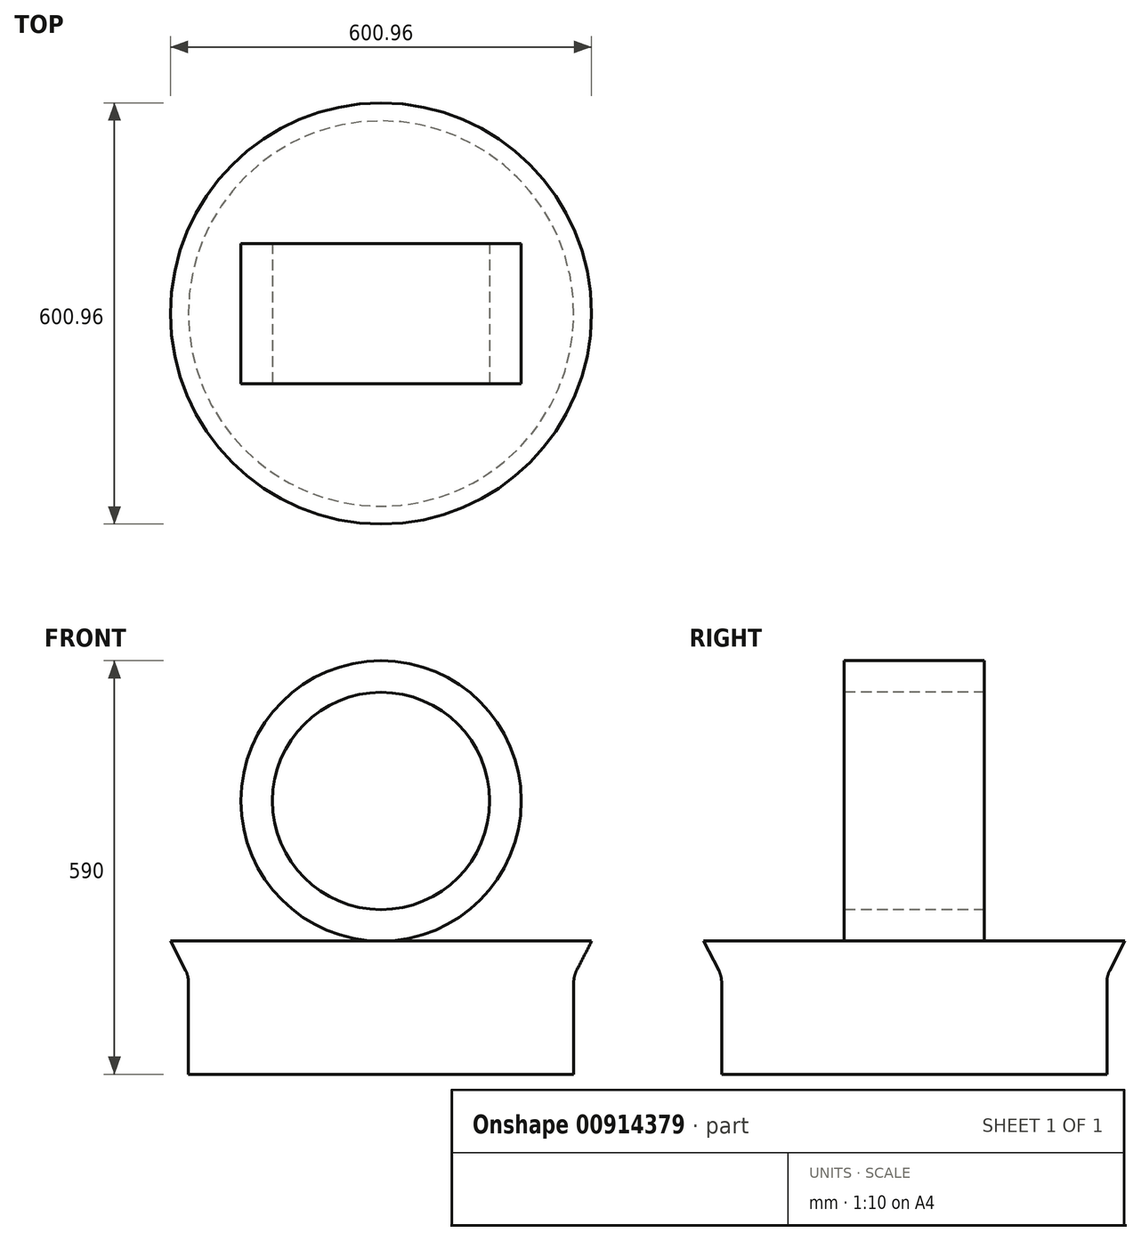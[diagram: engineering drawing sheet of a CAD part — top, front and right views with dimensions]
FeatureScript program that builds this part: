
annotation { "Feature Type Name" : "Feature", "Feature Type Description" : "" }
export const myFeature = defineFeature(function(context is Context, id is Id, definition is map)
    precondition{}
    {
        {
            var Q0;
            Q0=qCreatedBy(makeId("Top.planeOp"),FACE);
            var sketch = newSketch(context, id + "F0", { "sketchPlane" : qUnion([Q0])});
            skCircle(sketch, "E0", {"center": v(0, 0) * mm, "radius": 275 * mm});
            skSolve(sketch);
        }
        {
            var Q0;
            Q0 = qSketchRegion(id + "F0", true);
            extrude(context, id + "F1", {"entities" : qUnion([Q0]), "depth" : 140 * mm, "offsetDistance" : 25 * mm});
        }
        {
            var Q0;
            Q0=makeQuery(id+"F1.opExtrude","CAP_FACE",FACE,{"disambiguationData":[OSD([sQuery(id+"F0.wireOp",EDGE,"E0")])],"isStart":false});
            var sketch = newSketch(context, id + "F2", { "sketchPlane" : qUnion([Q0])});
            skCircle(sketch, "E1", {"center": v(0, 0) * mm, "radius": 275 * mm});
            skSolve(sketch);
        }
        {
            var Q0;
            Q0 = qSketchRegion(id + "F2", true);
            extrude(context, id + "F3", {"entities" : qUnion([Q0]), "operationType" : NewBodyOperationType.ADD, "depth" : 50 * mm, "offsetDistance" : 25 * mm, "hasDraft" : true, "draftAngle" : 27 * degree});
        }
        {
            var Q0;
            Q0=makeQuery(id+"F3.boolean.opBoolean","MERGE",EDGE,{"derivedFrom":[makeQuery(id+"F1.opExtrude","CAP_EDGE",EDGE,{"disambiguationData":[OSD([sQuery(id+"F0.wireOp",EDGE,"E0")])],"isStart":false}),makeQuery(id+"F3.opExtrude","CAP_EDGE",EDGE,{"disambiguationData":[OSD([sQuery(id+"F2.wireOp",EDGE,"E1")])],"isStart":true})]});
            fillet(context, id + "F4", {"entities" : qUnion([Q0]), "radius" : 35.2 * mm, "tangentPropagation" : true, "allowEdgeOverflow" : false});
        }
        {
            var Q0;
            Q0=qCreatedBy(makeId("Front.planeOp"),FACE);
            var sketch = newSketch(context, id + "F5", { "sketchPlane" : qUnion([Q0])});
            skLineSegment(sketch, "E2", {"start": v(0, 0) * mm, "end": v(0, 390) * mm});
            skCircle(sketch, "E3", {"center": v(0, 390) * mm, "radius": 200 * mm});
            skSolve(sketch);
        }
        {
            var Q0;
            Q0=qCreatedBy(makeId("Right.planeOp"),FACE);
            var sketch = newSketch(context, id + "F6", { "sketchPlane" : qUnion([Q0])});
            skLineSegment(sketch, "E4.bottom", {"start": v(100, 190) * mm, "end": v(-100, 190) * mm});
            skLineSegment(sketch, "E4.top", {"start": v(100, 235) * mm, "end": v(-100, 235) * mm});
            skLineSegment(sketch, "E4.left", {"start": v(100, 190) * mm, "end": v(100, 235) * mm});
            skLineSegment(sketch, "E4.right", {"start": v(-100, 190) * mm, "end": v(-100, 235) * mm});
            skPoint(sketch, "E4.middle", {"position": v(0, 212.5) * mm});
            skSolve(sketch);
        }
        {
            var Q0;
            Q0=makeQuery(id+"F6.imprint","IMPRINT",FACE,{"disambiguationData":[TD([[makeQuery(id+"F6.imprint","IMPRINT",EDGE,{"derivedFrom":sQuery(id+"F6.wireOp",EDGE,"E4.bottom")}),-1.0]])]});
            var Q1;
            Q1=sQuery(id+"F5.wireOp",EDGE,"E3");
            sweep(context, id + "F7", {"operationType" : NewBodyOperationType.ADD, "profiles" : qUnion([Q0]), "path" : qUnion([Q1])});
        }
    });
